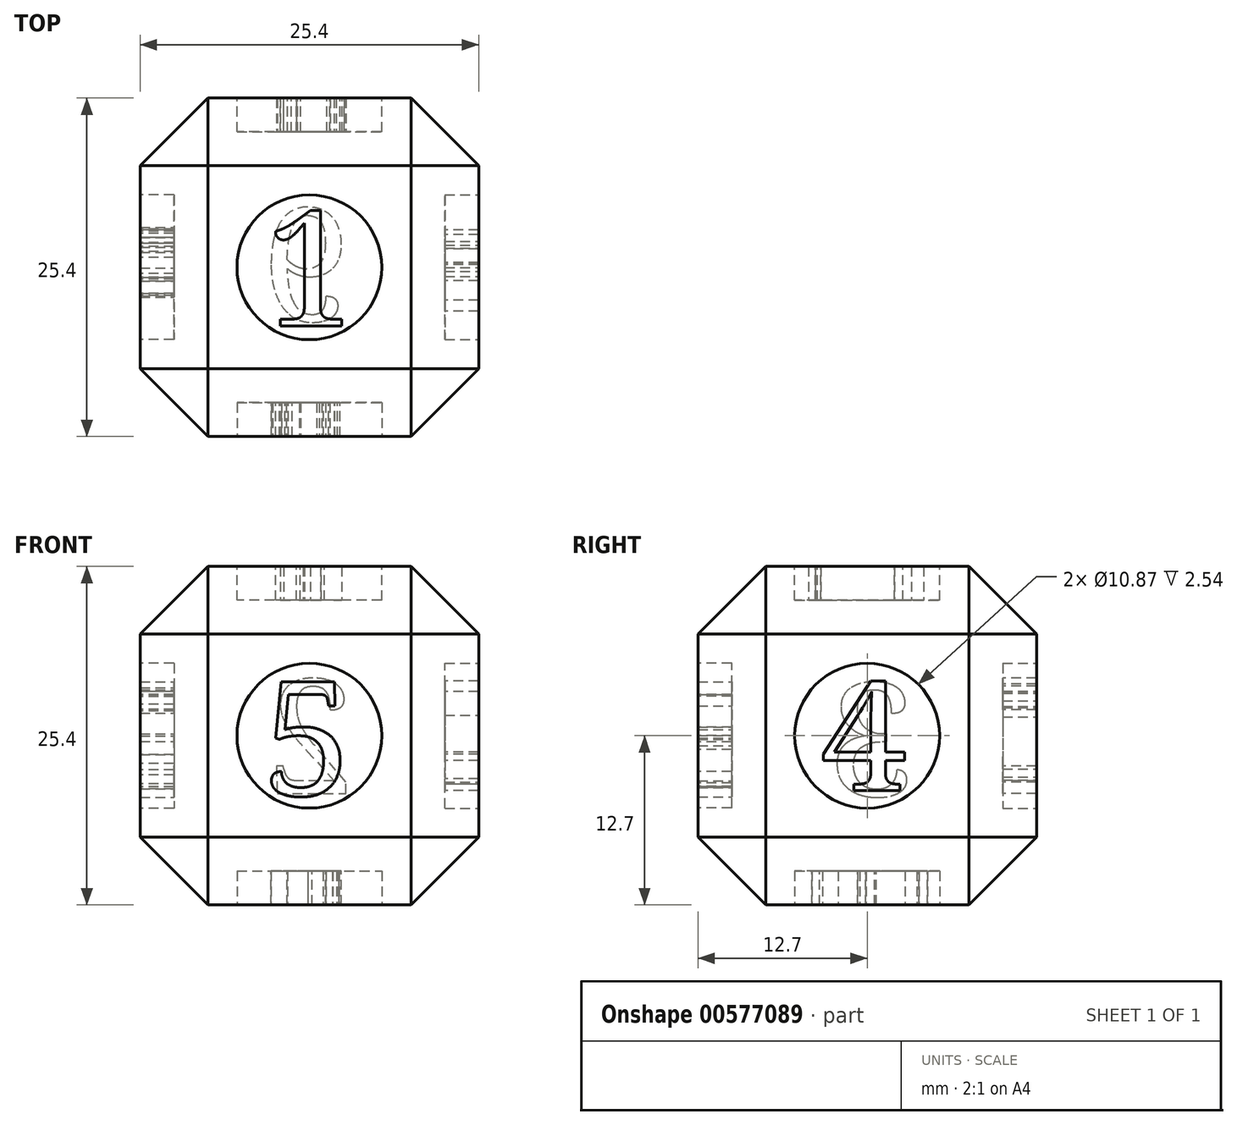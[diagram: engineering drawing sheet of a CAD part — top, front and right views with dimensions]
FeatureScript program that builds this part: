
annotation { "Feature Type Name" : "Feature", "Feature Type Description" : "" }
export const myFeature = defineFeature(function(context is Context, id is Id, definition is map)
    precondition{}
    {
        {
            var Q0;
            Q0=qCreatedBy(makeId("Front.planeOp"),FACE);
            var sketch = newSketch(context, id + "F0", { "sketchPlane" : qUnion([Q0])});
            skLineSegment(sketch, "E0.bottom", {"start": v(12.7, 12.7) * mm, "end": v(-12.7, 12.7) * mm});
            skLineSegment(sketch, "E0.top", {"start": v(12.7, -12.7) * mm, "end": v(-12.7, -12.7) * mm});
            skLineSegment(sketch, "E0.left", {"start": v(12.7, 12.7) * mm, "end": v(12.7, -12.7) * mm});
            skLineSegment(sketch, "E0.right", {"start": v(-12.7, 12.7) * mm, "end": v(-12.7, -12.7) * mm});
            skPoint(sketch, "E0.middle", {"position": v(0, 0) * mm});
            skSolve(sketch);
        }
        {
            var Q0;
            Q0=makeQuery(id+"F0.imprint","IMPRINT",FACE,{"disambiguationData":[TD([[makeQuery(id+"F0.imprint","IMPRINT",EDGE,{"derivedFrom":sQuery(id+"F0.wireOp",EDGE,"E0.bottom")}),1.0]])]});
            extrude(context, id + "F1", {"entities" : qUnion([Q0]), "depth" : 12.7 * mm, "offsetDistance" : 25.4 * mm});
        }
        {
            var Q0;
            Q0=makeQuery(id+"F1.opExtrude","CAP_FACE",FACE,{"disambiguationData":[OSD([sQuery(id+"F0.wireOp",EDGE,"E0.bottom"),sQuery(id+"F0.wireOp",EDGE,"E0.top"),sQuery(id+"F0.wireOp",EDGE,"E0.left"),sQuery(id+"F0.wireOp",EDGE,"E0.right")])],"isStart":true});
            extrude(context, id + "F2", {"entities" : qUnion([Q0]), "operationType" : NewBodyOperationType.ADD, "depth" : 12.7 * mm, "offsetDistance" : 25.4 * mm});
        }
        {
            var Q0;
            Q0=makeQuery(id+"F1.opExtrude","CAP_EDGE",EDGE,{"disambiguationData":[OSD([sQuery(id+"F0.wireOp",EDGE,"E0.left")])],"isStart":false});
            var Q1;
            Q1=makeQuery(id+"F1.opExtrude","CAP_EDGE",EDGE,{"disambiguationData":[OSD([sQuery(id+"F0.wireOp",EDGE,"E0.bottom")])],"isStart":false});
            var Q2;
            {var subQ0=sQuery(id+"F0.wireOp",EDGE,"E0.left");var subQ1=sQuery(id+"F0.wireOp",EDGE,"E0.bottom");Q2=makeQuery(id+"F2.boolean.opBoolean","MERGE",EDGE,{"derivedFrom":[makeQuery(id+"F1.opExtrude","SWEPT_EDGE",EDGE,{"disambiguationData":[OSD([subQ1,subQ0])]}),makeQuery(id+"F2.opExtrude","SWEPT_EDGE",EDGE,{"disambiguationData":[OSD([subQ1,subQ0])]})]});}
            var Q3;
            {var subQ0=sQuery(id+"F0.wireOp",EDGE,"E0.left");var subQ1=sQuery(id+"F0.wireOp",EDGE,"E0.top");Q3=makeQuery(id+"F2.boolean.opBoolean","MERGE",EDGE,{"derivedFrom":[makeQuery(id+"F1.opExtrude","SWEPT_EDGE",EDGE,{"disambiguationData":[OSD([subQ1,subQ0])]}),makeQuery(id+"F2.opExtrude","SWEPT_EDGE",EDGE,{"disambiguationData":[OSD([subQ1,subQ0])]})]});}
            var Q4;
            Q4=makeQuery(id+"F1.opExtrude","CAP_EDGE",EDGE,{"disambiguationData":[OSD([sQuery(id+"F0.wireOp",EDGE,"E0.right")])],"isStart":false});
            var Q5;
            Q5=makeQuery(id+"F1.opExtrude","CAP_EDGE",EDGE,{"disambiguationData":[OSD([sQuery(id+"F0.wireOp",EDGE,"E0.top")])],"isStart":false});
            var Q6;
            {var subQ0=sQuery(id+"F0.wireOp",EDGE,"E0.right");var subQ1=sQuery(id+"F0.wireOp",EDGE,"E0.bottom");Q6=makeQuery(id+"F2.boolean.opBoolean","MERGE",EDGE,{"derivedFrom":[makeQuery(id+"F1.opExtrude","SWEPT_EDGE",EDGE,{"disambiguationData":[OSD([subQ1,subQ0])]}),makeQuery(id+"F2.opExtrude","SWEPT_EDGE",EDGE,{"disambiguationData":[OSD([subQ1,subQ0])]})]});}
            var Q7;
            {var subQ0=sQuery(id+"F0.wireOp",EDGE,"E0.right");var subQ1=sQuery(id+"F0.wireOp",EDGE,"E0.top");Q7=makeQuery(id+"F2.boolean.opBoolean","MERGE",EDGE,{"derivedFrom":[makeQuery(id+"F1.opExtrude","SWEPT_EDGE",EDGE,{"disambiguationData":[OSD([subQ1,subQ0])]}),makeQuery(id+"F2.opExtrude","SWEPT_EDGE",EDGE,{"disambiguationData":[OSD([subQ1,subQ0])]})]});}
            var Q8;
            Q8=makeQuery(id+"F2.opExtrude","CAP_EDGE",EDGE,{"disambiguationData":[OSD([sQuery(id+"F0.wireOp",EDGE,"E0.bottom")])],"isStart":false});
            var Q9;
            Q9=makeQuery(id+"F2.opExtrude","CAP_EDGE",EDGE,{"disambiguationData":[OSD([sQuery(id+"F0.wireOp",EDGE,"E0.left")])],"isStart":false});
            var Q10;
            Q10=makeQuery(id+"F2.opExtrude","CAP_EDGE",EDGE,{"disambiguationData":[OSD([sQuery(id+"F0.wireOp",EDGE,"E0.top")])],"isStart":false});
            var Q11;
            Q11=makeQuery(id+"F2.opExtrude","CAP_EDGE",EDGE,{"disambiguationData":[OSD([sQuery(id+"F0.wireOp",EDGE,"E0.right")])],"isStart":false});
            chamfer(context, id + "F3", {"entities" : qUnion([Q0, Q1, Q2, Q3, Q4, Q5, Q6, Q7, Q8, Q9, Q10, Q11]), "width" : 5.08 * mm, "tangentPropagation" : true});
        }
        {
            var Q0;
            Q0=makeQuery(id+"F1.opExtrude","CAP_FACE",FACE,{"disambiguationData":[OSD([sQuery(id+"F0.wireOp",EDGE,"E0.bottom"),sQuery(id+"F0.wireOp",EDGE,"E0.top"),sQuery(id+"F0.wireOp",EDGE,"E0.left"),sQuery(id+"F0.wireOp",EDGE,"E0.right")])],"isStart":false});
            var sketch = newSketch(context, id + "F4", { "sketchPlane" : qUnion([Q0])});
            skCircle(sketch, "E1", {"center": v(0, 0) * mm, "radius": 5.43 * mm});
            skSolve(sketch);
        }
        {
            var Q0;
            Q0=makeQuery(id+"F4.imprint","IMPRINT",FACE,{"disambiguationData":[TD([[makeQuery(id+"F4.imprint","IMPRINT",EDGE,{"derivedFrom":sQuery(id+"F4.wireOp",EDGE,"E1")}),1.0]])]});
            extrude(context, id + "F5", {"entities" : qUnion([Q0]), "operationType" : NewBodyOperationType.REMOVE, "oppositeDirection" : true, "depth" : 2.54 * mm, "offsetDistance" : 25.4 * mm});
        }
        {
            var Q0;
            Q0=makeQuery(id+"F5.boolean.opBoolean","COPY",FACE,{"derivedFrom":makeQuery(id+"F5.opExtrude","CAP_FACE",FACE,{"disambiguationData":[OSD([sQuery(id+"F4.wireOp",EDGE,"E1")])],"isStart":false})});
            var sketch = newSketch(context, id + "F6", { "sketchPlane" : qUnion([Q0])});
            skText(sketch, "E2", { "text": "5", "fontName": "NotoSerif-Regular.ttf"});
            const initialGuessF6  = {"E2": [-0.00351, -0.00448, 1, 0, 0.00862]};
            skSetInitialGuess(sketch, initialGuessF6);
            skSolve(sketch);
        }
        {
            var Q0;
            Q0=makeQuery(id+"F2.opExtrude","CAP_FACE",FACE,{"disambiguationData":[OSD([sQuery(id+"F0.wireOp",EDGE,"E0.bottom"),sQuery(id+"F0.wireOp",EDGE,"E0.top"),sQuery(id+"F0.wireOp",EDGE,"E0.left"),sQuery(id+"F0.wireOp",EDGE,"E0.right")])],"isStart":false});
            var sketch = newSketch(context, id + "F7", { "sketchPlane" : qUnion([Q0])});
            skCircle(sketch, "E3", {"center": v(0, 0) * mm, "radius": 5.43 * mm});
            skSolve(sketch);
        }
        {
            var Q0;
            Q0=makeQuery(id+"F7.imprint","IMPRINT",FACE,{"disambiguationData":[TD([[makeQuery(id+"F7.imprint","IMPRINT",EDGE,{"derivedFrom":sQuery(id+"F7.wireOp",EDGE,"E3")}),1.0]])]});
            extrude(context, id + "F8", {"entities" : qUnion([Q0]), "operationType" : NewBodyOperationType.REMOVE, "oppositeDirection" : true, "depth" : 2.54 * mm, "offsetDistance" : 25.4 * mm});
        }
        {
            var Q0;
            Q0=makeQuery(id+"F8.boolean.opBoolean","COPY",FACE,{"derivedFrom":makeQuery(id+"F8.opExtrude","CAP_FACE",FACE,{"disambiguationData":[OSD([sQuery(id+"F7.wireOp",EDGE,"E3")])],"isStart":false})});
            var sketch = newSketch(context, id + "F9", { "sketchPlane" : qUnion([Q0])});
            skText(sketch, "E4", { "text": "2", "fontName": "NotoSerif-Regular.ttf"});
            const initialGuessF9  = {"E4": [-0.00335, -0.00435, 1, 0, 0.00863]};
            skSetInitialGuess(sketch, initialGuessF9);
            skSolve(sketch);
        }
        {
            var Q0;
            Q0=makeQuery(id+"F9.imprint","IMPRINT",FACE,{"disambiguationData":[TD([[makeQuery(id+"F9.imprint","IMPRINT",EDGE,{"derivedFrom":sQuery(id+"F9.wireOp",EDGE,"E4.sketch_text.stroke-0")}),-1.0]])]});
            extrude(context, id + "F10", {"entities" : qUnion([Q0]), "operationType" : NewBodyOperationType.ADD, "depth" : 2.54 * mm, "offsetDistance" : 25.4 * mm});
        }
        {
            var Q0;
            {var subQ0=sQuery(id+"F0.wireOp",EDGE,"E0.bottom");Q0=makeQuery(id+"F2.boolean.opBoolean","MERGE",FACE,{"derivedFrom":[makeQuery(id+"F1.opExtrude","SWEPT_FACE",FACE,{"disambiguationData":[OSD([subQ0])]}),makeQuery(id+"F2.opExtrude","SWEPT_FACE",FACE,{"disambiguationData":[OSD([subQ0])]})]});}
            var sketch = newSketch(context, id + "F11", { "sketchPlane" : qUnion([Q0])});
            skCircle(sketch, "E5", {"center": v(0, 0) * mm, "radius": 5.44 * mm});
            skSolve(sketch);
        }
        {
            var Q0;
            Q0=makeQuery(id+"F11.imprint","IMPRINT",FACE,{"disambiguationData":[TD([[makeQuery(id+"F11.imprint","IMPRINT",EDGE,{"derivedFrom":sQuery(id+"F11.wireOp",EDGE,"E5")}),1.0]])]});
            extrude(context, id + "F12", {"entities" : qUnion([Q0]), "operationType" : NewBodyOperationType.REMOVE, "oppositeDirection" : true, "depth" : 2.54 * mm, "offsetDistance" : 25.4 * mm});
        }
        {
            var Q0;
            Q0=makeQuery(id+"F12.boolean.opBoolean","COPY",FACE,{"derivedFrom":makeQuery(id+"F12.opExtrude","CAP_FACE",FACE,{"disambiguationData":[OSD([sQuery(id+"F11.wireOp",EDGE,"E5")])],"isStart":false})});
            var sketch = newSketch(context, id + "F13", { "sketchPlane" : qUnion([Q0])});
            skText(sketch, "E6", { "text": "1", "fontName": "NotoSerif-Regular.ttf"});
            const initialGuessF13  = {"E6": [-0.00334, -0.0044, 1, 0, 0.00868]};
            skSetInitialGuess(sketch, initialGuessF13);
            skSolve(sketch);
        }
        {
            var Q0;
            Q0=makeQuery(id+"F13.imprint","IMPRINT",FACE,{"disambiguationData":[TD([[makeQuery(id+"F13.imprint","IMPRINT",EDGE,{"derivedFrom":sQuery(id+"F13.wireOp",EDGE,"E6.sketch_text.stroke-0")}),-1.0]])]});
            extrude(context, id + "F14", {"entities" : qUnion([Q0]), "operationType" : NewBodyOperationType.ADD, "depth" : 2.54 * mm, "offsetDistance" : 25.4 * mm});
        }
        {
            var Q0;
            {var subQ0=sQuery(id+"F0.wireOp",EDGE,"E0.top");Q0=makeQuery(id+"F2.boolean.opBoolean","MERGE",FACE,{"derivedFrom":[makeQuery(id+"F1.opExtrude","SWEPT_FACE",FACE,{"disambiguationData":[OSD([subQ0])]}),makeQuery(id+"F2.opExtrude","SWEPT_FACE",FACE,{"disambiguationData":[OSD([subQ0])]})]});}
            var sketch = newSketch(context, id + "F15", { "sketchPlane" : qUnion([Q0])});
            skCircle(sketch, "E7", {"center": v(0, 0) * mm, "radius": 5.44 * mm});
            skSolve(sketch);
        }
        {
            var Q0;
            Q0=makeQuery(id+"F15.imprint","IMPRINT",FACE,{"disambiguationData":[TD([[makeQuery(id+"F15.imprint","IMPRINT",EDGE,{"derivedFrom":sQuery(id+"F15.wireOp",EDGE,"E7")}),1.0]])]});
            extrude(context, id + "F16", {"entities" : qUnion([Q0]), "operationType" : NewBodyOperationType.REMOVE, "oppositeDirection" : true, "depth" : 2.54 * mm, "offsetDistance" : 25.4 * mm});
        }
        {
            var Q0;
            Q0=makeQuery(id+"F16.boolean.opBoolean","COPY",FACE,{"derivedFrom":makeQuery(id+"F16.opExtrude","CAP_FACE",FACE,{"disambiguationData":[OSD([sQuery(id+"F15.wireOp",EDGE,"E7")])],"isStart":false})});
            var sketch = newSketch(context, id + "F17", { "sketchPlane" : qUnion([Q0])});
            skText(sketch, "E8", { "text": "6", "fontName": "NotoSerif-Regular.ttf"});
            const initialGuessF17  = {"E8": [-0.00359, -0.00441, 1, 0, 0.0085]};
            skSetInitialGuess(sketch, initialGuessF17);
            skSolve(sketch);
        }
        {
            var Q0;
            Q0 = qSketchRegion(id + "F17", true);
            extrude(context, id + "F18", {"entities" : qUnion([Q0]), "operationType" : NewBodyOperationType.ADD, "depth" : 2.54 * mm, "offsetDistance" : 25.4 * mm});
        }
        {
            var Q0;
            Q0 = qSketchRegion(id + "F6", true);
            extrude(context, id + "F19", {"entities" : qUnion([Q0]), "operationType" : NewBodyOperationType.ADD, "depth" : 2.54 * mm, "offsetDistance" : 25.4 * mm});
        }
        {
            var Q0;
            {var subQ0=sQuery(id+"F0.wireOp",EDGE,"E0.right");Q0=makeQuery(id+"F2.boolean.opBoolean","MERGE",FACE,{"derivedFrom":[makeQuery(id+"F1.opExtrude","SWEPT_FACE",FACE,{"disambiguationData":[OSD([subQ0])]}),makeQuery(id+"F2.opExtrude","SWEPT_FACE",FACE,{"disambiguationData":[OSD([subQ0])]})]});}
            var sketch = newSketch(context, id + "F20", { "sketchPlane" : qUnion([Q0])});
            skCircle(sketch, "E9", {"center": v(0, 0) * mm, "radius": 5.44 * mm});
            skSolve(sketch);
        }
        {
            var Q0;
            Q0=makeQuery(id+"F20.imprint","IMPRINT",FACE,{"disambiguationData":[TD([[makeQuery(id+"F20.imprint","IMPRINT",EDGE,{"derivedFrom":sQuery(id+"F20.wireOp",EDGE,"E9")}),1.0]])]});
            extrude(context, id + "F21", {"entities" : qUnion([Q0]), "operationType" : NewBodyOperationType.REMOVE, "oppositeDirection" : true, "depth" : 2.54 * mm, "offsetDistance" : 25.4 * mm});
        }
        {
            var Q0;
            Q0=makeQuery(id+"F21.boolean.opBoolean","COPY",FACE,{"derivedFrom":makeQuery(id+"F21.opExtrude","CAP_FACE",FACE,{"disambiguationData":[OSD([sQuery(id+"F20.wireOp",EDGE,"E9")])],"isStart":false})});
            var sketch = newSketch(context, id + "F22", { "sketchPlane" : qUnion([Q0])});
            skText(sketch, "E10", { "text": "3", "fontName": "NotoSerif-Regular.ttf"});
            const initialGuessF22  = {"E10": [-0.00367, -0.00452, 1, 0, 0.00852]};
            skSetInitialGuess(sketch, initialGuessF22);
            skSolve(sketch);
        }
        {
            var Q0;
            Q0 = qSketchRegion(id + "F22", true);
            extrude(context, id + "F23", {"entities" : qUnion([Q0]), "operationType" : NewBodyOperationType.ADD, "depth" : 2.54 * mm, "offsetDistance" : 25.4 * mm});
        }
        {
            var Q0;
            {var subQ0=sQuery(id+"F0.wireOp",EDGE,"E0.left");Q0=makeQuery(id+"F2.boolean.opBoolean","MERGE",FACE,{"derivedFrom":[makeQuery(id+"F1.opExtrude","SWEPT_FACE",FACE,{"disambiguationData":[OSD([subQ0])]}),makeQuery(id+"F2.opExtrude","SWEPT_FACE",FACE,{"disambiguationData":[OSD([subQ0])]})]});}
            var sketch = newSketch(context, id + "F24", { "sketchPlane" : qUnion([Q0])});
            skCircle(sketch, "E11", {"center": v(0, 0) * mm, "radius": 5.44 * mm});
            skSolve(sketch);
        }
        {
            var Q0;
            Q0=makeQuery(id+"F24.imprint","IMPRINT",FACE,{"disambiguationData":[TD([[makeQuery(id+"F24.imprint","IMPRINT",EDGE,{"derivedFrom":sQuery(id+"F24.wireOp",EDGE,"E11")}),1.0]])]});
            extrude(context, id + "F25", {"entities" : qUnion([Q0]), "operationType" : NewBodyOperationType.REMOVE, "oppositeDirection" : true, "depth" : 2.54 * mm, "offsetDistance" : 25.4 * mm});
        }
        {
            var Q0;
            Q0=makeQuery(id+"F25.boolean.opBoolean","COPY",FACE,{"derivedFrom":makeQuery(id+"F25.opExtrude","CAP_FACE",FACE,{"disambiguationData":[OSD([sQuery(id+"F24.wireOp",EDGE,"E11")])],"isStart":false})});
            var sketch = newSketch(context, id + "F26", { "sketchPlane" : qUnion([Q0])});
            skText(sketch, "E12", { "text": "4", "fontName": "NotoSerif-Regular.ttf"});
            const initialGuessF26  = {"E12": [-0.00348, -0.00412, 1, 0, 0.0083]};
            skSetInitialGuess(sketch, initialGuessF26);
            skSolve(sketch);
        }
        {
            var Q0;
            Q0=makeQuery(id+"F26.imprint","IMPRINT",FACE,{"disambiguationData":[TD([[makeQuery(id+"F26.imprint","IMPRINT",EDGE,{"derivedFrom":sQuery(id+"F26.wireOp",EDGE,"E12.sketch_text.stroke-0")}),-1.0]])]});
            extrude(context, id + "F27", {"entities" : qUnion([Q0]), "operationType" : NewBodyOperationType.ADD, "depth" : 2.54 * mm, "offsetDistance" : 25.4 * mm});
        }
    });
